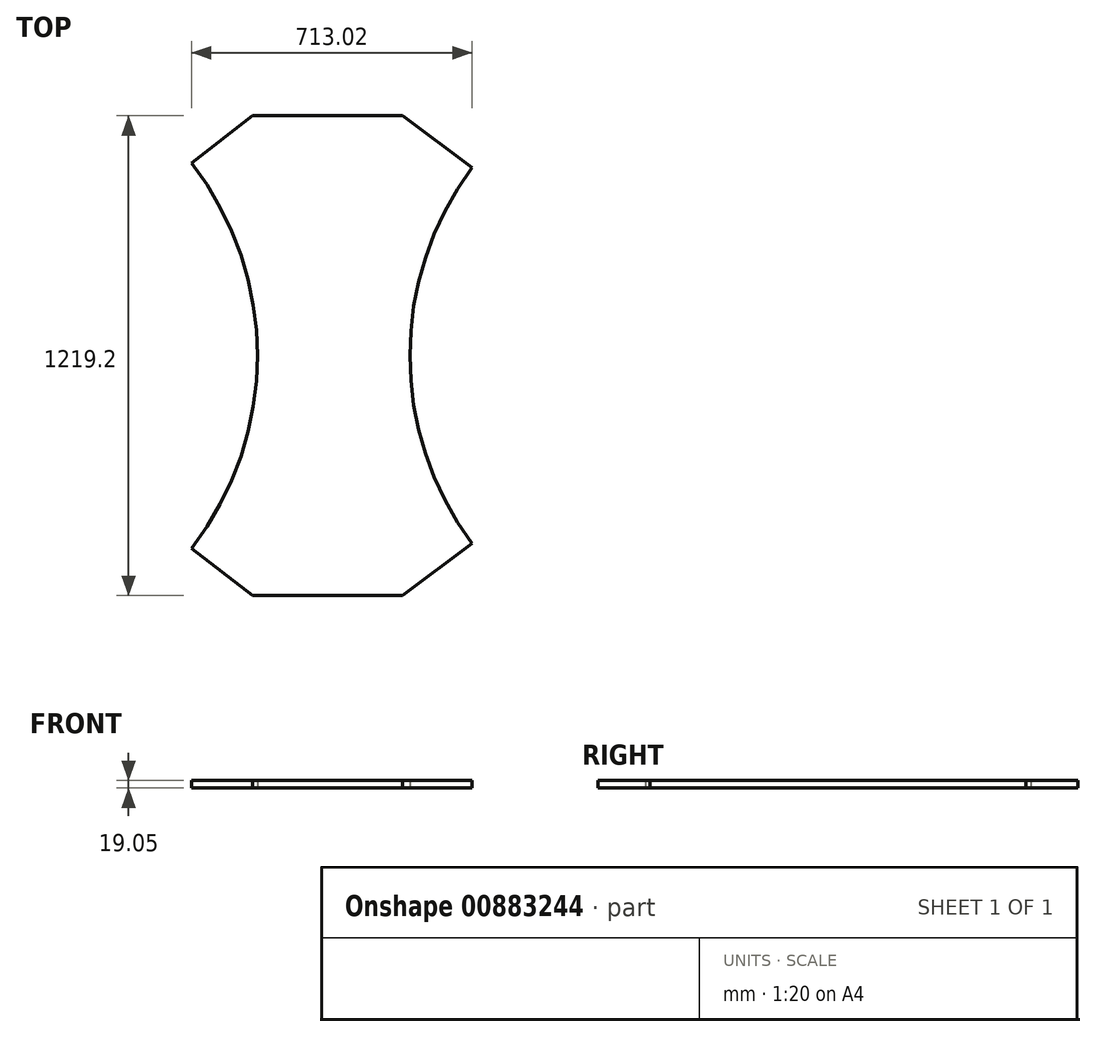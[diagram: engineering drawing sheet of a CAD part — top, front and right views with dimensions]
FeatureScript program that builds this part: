
annotation { "Feature Type Name" : "Feature", "Feature Type Description" : "" }
export const myFeature = defineFeature(function(context is Context, id is Id, definition is map)
    precondition{}
    {
        {
            var Q0;
            Q0=qCreatedBy(makeId("Top.planeOp"),FACE);
            var sketch = newSketch(context, id + "F0", { "sketchPlane" : qUnion([Q0])});
            skLineSegment(sketch, "E0", {"start": v(0, -609.6) * mm, "end": v(0, 609.6) * mm, "construction": true});
            skLineSegment(sketch, "E1.bottom", {"start": v(0, -609.6) * mm, "end": v(-190.5, -609.6) * mm});
            skLineSegment(sketch, "E1.top", {"start": v(0, 609.6) * mm, "end": v(-190.5, 609.6) * mm});
            skLineSegment(sketch, "E2.MirrorCS", {"start": v(0, -609.6) * mm, "end": v(190.5, -609.6) * mm});
            skLineSegment(sketch, "E3.MirrorCS", {"start": v(0, 609.6) * mm, "end": v(190.5, 609.6) * mm});
            skCircle(sketch, "E4", {"center": v(-977.9, 0) * mm, "radius": 774.7 * mm, "construction": true});
            skCircle(sketch, "E5.MirrorC", {"center": v(1009.65, 0) * mm, "radius": 774.7 * mm, "construction": true});
            skArc(sketch, "E6.0", {"start": v(-345.24, -489.8) * mm, "mid": v(-177.8, 0) * mm, "end": v(-345.24, 489.8) * mm});
            skArc(sketch, "E7.0", {"start": v(367.78, -477.67) * mm, "mid": v(209.55, 0) * mm, "end": v(367.78, 477.67) * mm});
            skLineSegment(sketch, "E8", {"start": v(-190.5, 609.6) * mm, "end": v(-345.24, 489.8) * mm});
            skLineSegment(sketch, "E9", {"start": v(190.5, 609.6) * mm, "end": v(367.78, 477.67) * mm});
            skLineSegment(sketch, "E10", {"start": v(-190.5, -609.6) * mm, "end": v(-345.24, -489.8) * mm});
            skLineSegment(sketch, "E11", {"start": v(190.5, -609.6) * mm, "end": v(367.78, -477.67) * mm});
            skSolve(sketch);
        }
        {
            var Q0;
            Q0 = qSketchRegion(id + "F0", true);
            extrude(context, id + "F1", {"entities" : qUnion([Q0]), "depth" : 19.05 * mm, "offsetDistance" : 25.4 * mm});
        }
    });
